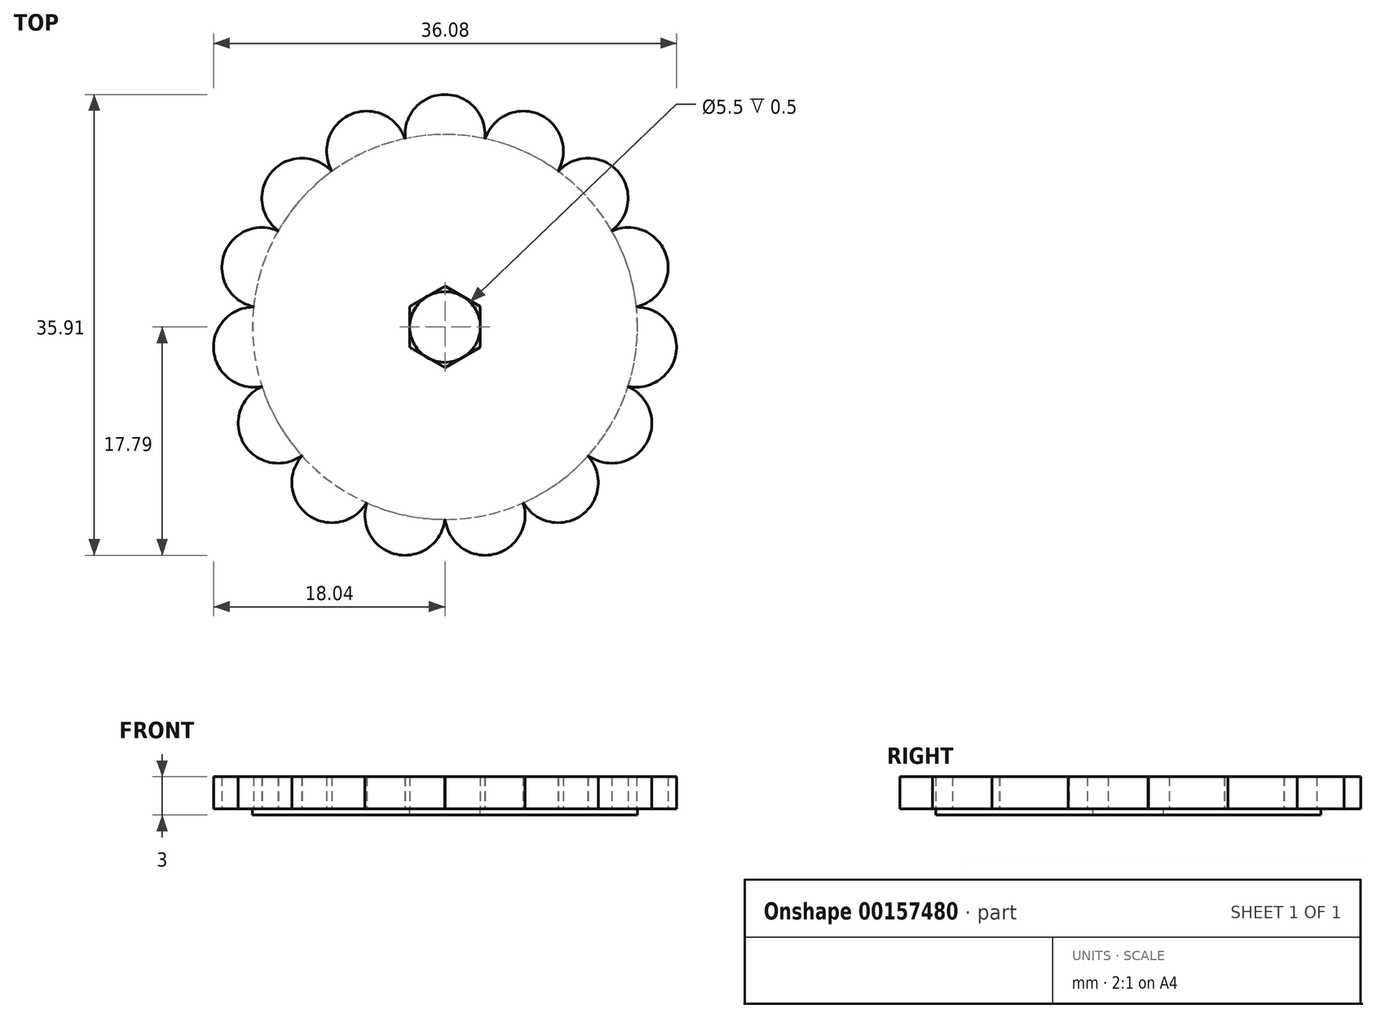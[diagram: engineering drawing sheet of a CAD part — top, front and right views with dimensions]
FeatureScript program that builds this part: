
annotation { "Feature Type Name" : "Feature", "Feature Type Description" : "" }
export const myFeature = defineFeature(function(context is Context, id is Id, definition is map)
    precondition{}
    {
        {
            var Q0;
            Q0=qCreatedBy(makeId("Top.planeOp"),FACE);
            var sketch = newSketch(context, id + "F0", { "sketchPlane" : qUnion([Q0])});
            skCircle(sketch, "E0.cCircle", {"center": v(0, 0) * mm, "radius": 2.75 * mm});
            skLineSegment(sketch, "E0.0", {"start": v(2.75, 1.59) * mm, "end": v(2.75, -1.59) * mm});
            skLineSegment(sketch, "E0.1", {"start": v(2.75, -1.59) * mm, "end": v(0, -3.18) * mm});
            skLineSegment(sketch, "E0.2", {"start": v(0, -3.18) * mm, "end": v(-2.75, -1.59) * mm});
            skLineSegment(sketch, "E0.3", {"start": v(-2.75, -1.59) * mm, "end": v(-2.75, 1.59) * mm});
            skLineSegment(sketch, "E0.4", {"start": v(-2.75, 1.59) * mm, "end": v(0, 3.18) * mm});
            skLineSegment(sketch, "E0.5", {"start": v(0, 3.18) * mm, "end": v(2.75, 1.59) * mm});
            skPoint(sketch, "E0.0.midPoint", {"position": v(2.75, 0) * mm});
            skCircle(sketch, "E1", {"center": v(0, 0) * mm, "radius": 15 * mm});
            skLineSegment(sketch, "E2", {"start": v(0, 0) * mm, "end": v(0, 21.86) * mm, "construction": true});
            skLineSegment(sketch, "E3", {"start": v(0, 0) * mm, "end": v(4.65, 21.86) * mm, "construction": true});
            skLineSegment(sketch, "E4", {"start": v(0, 0) * mm, "end": v(5.7, 12.78) * mm, "construction": true});
            skPoint(sketch, "E5.center", {"position": v(0, 4) * mm});
            skLineSegment(sketch, "E5.anchor1", {"start": v(0, 4) * mm, "end": v(0, 15) * mm, "construction": true});
            skLineSegment(sketch, "E5.anchor2", {"start": v(0, 4) * mm, "end": v(0, 15) * mm, "construction": true});
            skArc(sketch, "E6", {"start": v(3.05, 14.35) * mm, "mid": v(0.16, 18.11) * mm, "end": v(-3.1, 14.68) * mm});
            skSolve(sketch);
        }
        {
            var Q0;
            Q0=makeQuery(id+"F0.imprint","IMPRINT",FACE,{"disambiguationData":[TD([[makeQuery(id+"F0.imprint","IMPRINT",EDGE,{"derivedFrom":sQuery(id+"F0.wireOp",EDGE,"E0.0")}),1.0]])]});
            extrude(context, id + "F1", {"entities" : qUnion([Q0]), "depth" : 2.5 * mm});
        }
        {
            var Q0;
            {var subQ31=sQuery(id+"F0.wireOp",EDGE,"E0.5");var subQ36=sQuery(id+"F0.wireOp",EDGE,"E0.0");var subQ40=makeQuery(id+"F0.imprint","INTERSECT",VERTEX,{"derivedFrom":[subQ36,subQ31]});Q0=makeQuery(id+"F0.imprint","IMPRINT",FACE,{"disambiguationData":[TD([[makeQuery(id+"F0.imprint","IMPRINT",EDGE,{"disambiguationData":[TD([[subQ40,-1.0]])],"derivedFrom":subQ36}),1.0]])]});}
            var Q1;
            {var subQ0=sQuery(id+"F0.wireOp",EDGE,"E0.3");var subQ1=sQuery(id+"F0.wireOp",EDGE,"E0.cCircle");var subQ2=makeQuery(id+"F0.imprint","INTERSECT",VERTEX,{"derivedFrom":[subQ1,subQ0]});Q1=makeQuery(id+"F0.imprint","IMPRINT",FACE,{"disambiguationData":[TD([[makeQuery(id+"F0.imprint","IMPRINT",EDGE,{"disambiguationData":[TD([[subQ2,-1.0]])],"derivedFrom":subQ1}),-1.0]])]});}
            var Q2;
            {var subQ0=sQuery(id+"F0.wireOp",EDGE,"E0.4");var subQ1=sQuery(id+"F0.wireOp",EDGE,"E0.cCircle");var subQ2=makeQuery(id+"F0.imprint","INTERSECT",VERTEX,{"derivedFrom":[subQ1,subQ0]});Q2=makeQuery(id+"F0.imprint","IMPRINT",FACE,{"disambiguationData":[TD([[makeQuery(id+"F0.imprint","IMPRINT",EDGE,{"disambiguationData":[TD([[subQ2,-1.0]])],"derivedFrom":subQ1}),-1.0]])]});}
            var Q3;
            {var subQ0=sQuery(id+"F0.wireOp",EDGE,"E0.5");var subQ1=sQuery(id+"F0.wireOp",EDGE,"E0.cCircle");var subQ2=makeQuery(id+"F0.imprint","INTERSECT",VERTEX,{"derivedFrom":[subQ1,subQ0]});Q3=makeQuery(id+"F0.imprint","IMPRINT",FACE,{"disambiguationData":[TD([[makeQuery(id+"F0.imprint","IMPRINT",EDGE,{"disambiguationData":[TD([[subQ2,-1.0]])],"derivedFrom":subQ1}),-1.0]])]});}
            var Q4;
            {var subQ0=sQuery(id+"F0.wireOp",EDGE,"E0.5");var subQ1=sQuery(id+"F0.wireOp",EDGE,"E0.cCircle");var subQ2=makeQuery(id+"F0.imprint","INTERSECT",VERTEX,{"derivedFrom":[subQ1,subQ0]});Q4=makeQuery(id+"F0.imprint","IMPRINT",FACE,{"disambiguationData":[TD([[makeQuery(id+"F0.imprint","IMPRINT",EDGE,{"disambiguationData":[TD([[subQ2,1.0]])],"derivedFrom":subQ1}),-1.0]])]});}
            var Q5;
            {var subQ0=sQuery(id+"F0.wireOp",EDGE,"E0.0");var subQ1=sQuery(id+"F0.wireOp",EDGE,"E0.cCircle");var subQ2=makeQuery(id+"F0.imprint","INTERSECT",VERTEX,{"derivedFrom":[subQ1,subQ0]});Q5=makeQuery(id+"F0.imprint","IMPRINT",FACE,{"disambiguationData":[TD([[makeQuery(id+"F0.imprint","IMPRINT",EDGE,{"disambiguationData":[TD([[subQ2,1.0]])],"derivedFrom":subQ1}),-1.0]])]});}
            var Q6;
            {var subQ0=sQuery(id+"F0.wireOp",EDGE,"E0.2");var subQ1=sQuery(id+"F0.wireOp",EDGE,"E0.cCircle");var subQ2=makeQuery(id+"F0.imprint","INTERSECT",VERTEX,{"derivedFrom":[subQ1,subQ0]});Q6=makeQuery(id+"F0.imprint","IMPRINT",FACE,{"disambiguationData":[TD([[makeQuery(id+"F0.imprint","IMPRINT",EDGE,{"disambiguationData":[TD([[subQ2,-1.0]])],"derivedFrom":subQ1}),-1.0]])]});}
            extrude(context, id + "F2", {"entities" : qUnion([Q0, Q1, Q2, Q3, Q4, Q5, Q6]), "operationType" : NewBodyOperationType.ADD, "oppositeDirection" : true, "depth" : .5 * mm});
        }
        {
            var Q0;
            {var subQ0=sQuery(id+"F0.wireOp",EDGE,"E6");var subQ1=sQuery(id+"F0.wireOp",EDGE,"E1");var subQ2=makeQuery(id+"F0.imprint","INTERSECT",VERTEX,{"disambiguationData":[OD(0.0)],"derivedFrom":[subQ1,subQ0]});Q0=makeQuery(id+"F0.imprint","IMPRINT",FACE,{"disambiguationData":[TD([[makeQuery(id+"F0.imprint","IMPRINT",EDGE,{"disambiguationData":[TD([[subQ2,1.0]])],"derivedFrom":subQ1}),-1.0]])]});}
            var Q1;
            Q1=makeQuery(id+"F1.opExtrude","CAP_FACE",FACE,{"disambiguationData":[OSD([sQuery(id+"F0.wireOp",EDGE,"E0.0"),sQuery(id+"F0.wireOp",EDGE,"E0.1"),sQuery(id+"F0.wireOp",EDGE,"E0.2"),sQuery(id+"F0.wireOp",EDGE,"E0.3"),sQuery(id+"F0.wireOp",EDGE,"E0.4"),sQuery(id+"F0.wireOp",EDGE,"E0.5"),sQuery(id+"F0.wireOp",EDGE,"E1")])],"isStart":false});
            extrude(context, id + "F4", {"entities" : qUnion([Q0]), "endBound" : BoundingType.UP_TO_SURFACE, "endBoundEntityFace" : qUnion([Q1]), "depth" : 25 * mm});
        }
        {
            var Q0;
            Q0=makeQuery(id+"F4.opExtrude","SWEPT_BODY",BODY,{"disambiguationData":[OSD([sQuery(id+"F0.wireOp",EDGE,"E1"),sQuery(id+"F0.wireOp",EDGE,"E6")])]});
            var Q1;
            Q1=makeQuery(id+"F1.opExtrude","CAP_EDGE",EDGE,{"disambiguationData":[OSD([sQuery(id+"F0.wireOp",EDGE,"E1")])],"isStart":false});
            circularPattern(context, id + "F3", {"operationType" : NewBodyOperationType.ADD, "entities" : qUnion([Q0]), "axis" : qUnion([Q1]), "angle" : 360 * degree, "instanceCount" : 15, "equalSpace" : true});
        }
    });
